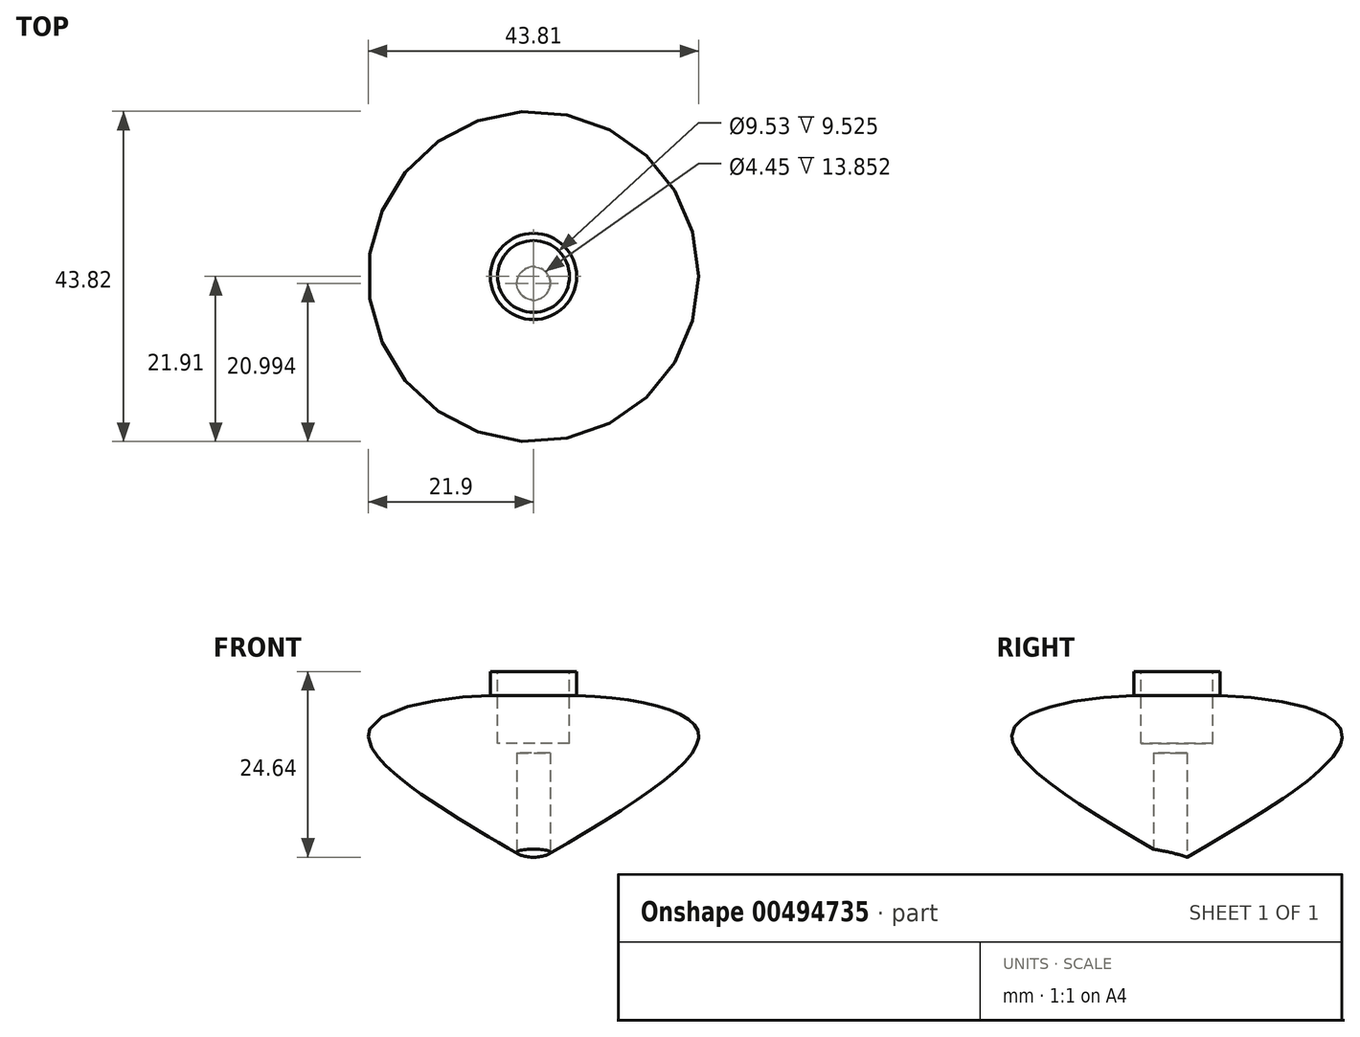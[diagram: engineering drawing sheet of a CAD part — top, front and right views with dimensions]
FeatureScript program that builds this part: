
annotation { "Feature Type Name" : "Feature", "Feature Type Description" : "" }
export const myFeature = defineFeature(function(context is Context, id is Id, definition is map)
    precondition{}
    {
        {
            var Q0;
            Q0=qCreatedBy(makeId("Front.planeOp"),FACE);
            var sketch = newSketch(context, id + "F0", { "sketchPlane" : qUnion([Q0])});
            skFitSpline(sketch, "E0", {"points": [v(0, 0) * mm, v(21.9, 17.1) * mm, v(5.72, 22.23) * mm], "startDerivative": vector(61.27, 35.44) * mm, "endDerivative": vector(-57.57, 2.25) * mm});
            skLineSegment(sketch, "E1", {"start": v(5.72, 22.23) * mm, "end": v(5.72, 25.4) * mm});
            skLineSegment(sketch, "E2", {"start": v(5.72, 25.4) * mm, "end": v(0, 25.4) * mm});
            skLineSegment(sketch, "E3", {"start": v(0, 25.4) * mm, "end": v(0, 0) * mm});
            skSolve(sketch);
        }
        {
            var Q0;
            Q0 = qSketchRegion(id + "F0", true);
            var Q1;
            Q1 = qSketchRegion(id + "F2", true);
            var Q2;
            Q2=sQuery(id+"F0.wireOp",EDGE,"E3");
            revolve(context, id + "F1", {"entities" : qUnion([Q0, Q1]), "axis" : qUnion([Q2]), "revolveType" : RevolveType.FULL});
        }
        {
            var Q0;
            Q0=makeQuery(id+"F1.opRevolve","SWEPT_FACE",FACE,{"disambiguationData":[OSD([sQuery(id+"F0.wireOp",EDGE,"E2")])]});
            var sketch = newSketch(context, id + "F2", { "sketchPlane" : qUnion([Q0])});
            skCircle(sketch, "E4", {"center": v(0, 0) * mm, "radius": 4.76 * mm});
            skSolve(sketch);
        }
        {
            var Q0;
            Q0 = qSketchRegion(id + "F2", true);
            extrude(context, id + "F3", {"entities" : qUnion([Q0]), "operationType" : NewBodyOperationType.REMOVE, "oppositeDirection" : true, "depth" : 9.52 * mm});
        }
        {
            var Q0;
            Q0=qCreatedBy(makeId("Top.planeOp"),FACE);
            var sketch = newSketch(context, id + "F4", { "sketchPlane" : qUnion([Q0])});
            skCircle(sketch, "E5", {"center": v(0, -0.92) * mm, "radius": 2.22 * mm});
            skSolve(sketch);
        }
        {
            var Q0;
            Q0 = qSketchRegion(id + "F4", true);
            extrude(context, id + "F5", {"entities" : qUnion([Q0]), "operationType" : NewBodyOperationType.REMOVE, "depth" : 14.6 * mm});
        }
    });
